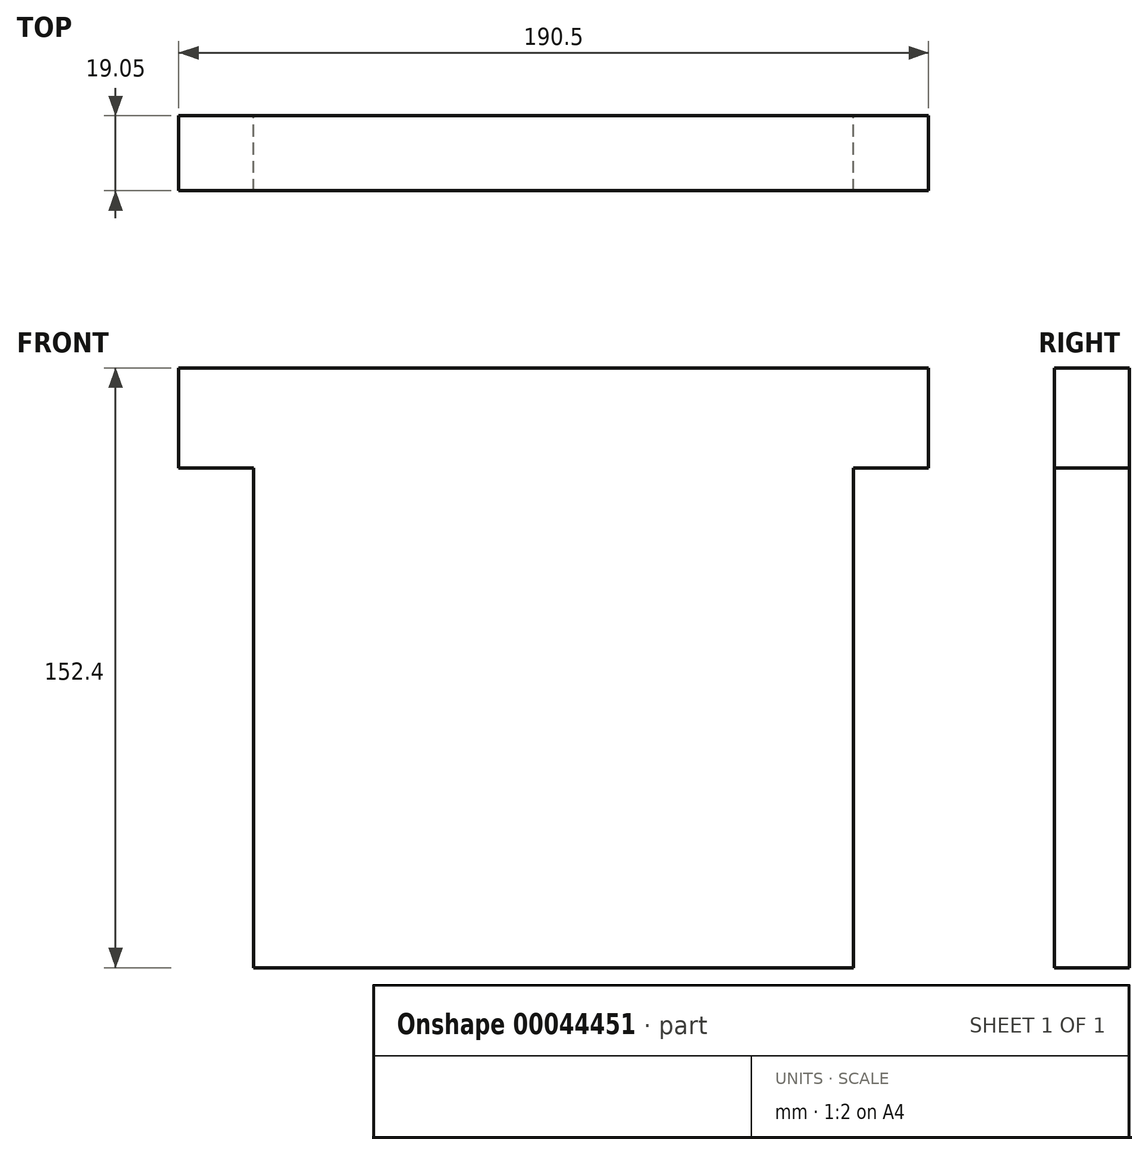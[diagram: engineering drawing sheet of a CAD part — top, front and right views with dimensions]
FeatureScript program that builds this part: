
annotation { "Feature Type Name" : "Feature", "Feature Type Description" : "" }
export const myFeature = defineFeature(function(context is Context, id is Id, definition is map)
    precondition{}
    {
        {
            var Q0;
            Q0=qCreatedBy(makeId("Front.planeOp"),FACE);
            var sketch = newSketch(context, id + "F0", { "sketchPlane" : qUnion([Q0])});
            skLineSegment(sketch, "E0.bottom", {"start": v(-66.37, 67.72) * mm, "end": v(86.03, 67.72) * mm});
            skLineSegment(sketch, "E0.top", {"start": v(-66.37, -84.68) * mm, "end": v(86.03, -84.68) * mm});
            skLineSegment(sketch, "E0.left", {"start": v(-66.37, 67.72) * mm, "end": v(-66.37, -84.68) * mm});
            skLineSegment(sketch, "E0.right", {"start": v(86.03, 67.72) * mm, "end": v(86.03, -84.68) * mm});
            skLineSegment(sketch, "E1.bottom", {"start": v(-66.37, 67.72) * mm, "end": v(-85.42, 67.72) * mm});
            skLineSegment(sketch, "E1.top", {"start": v(-66.37, 42.32) * mm, "end": v(-85.42, 42.32) * mm});
            skLineSegment(sketch, "E1.left", {"start": v(-66.37, 67.72) * mm, "end": v(-66.37, 42.32) * mm});
            skLineSegment(sketch, "E1.right", {"start": v(-85.42, 67.72) * mm, "end": v(-85.42, 42.32) * mm});
            skLineSegment(sketch, "E2.bottom", {"start": v(86.03, 67.72) * mm, "end": v(105.08, 67.72) * mm});
            skLineSegment(sketch, "E2.top", {"start": v(86.03, 42.32) * mm, "end": v(105.08, 42.32) * mm});
            skLineSegment(sketch, "E2.left", {"start": v(86.03, 67.72) * mm, "end": v(86.03, 42.32) * mm});
            skLineSegment(sketch, "E2.right", {"start": v(105.08, 67.72) * mm, "end": v(105.08, 42.32) * mm});
            skSolve(sketch);
        }
        {
            var Q0;
            Q0=makeQuery(id+"F0.imprint","IMPRINT",FACE,{"disambiguationData":[TD([[makeQuery(id+"F0.imprint","IMPRINT",EDGE,{"derivedFrom":sQuery(id+"F0.wireOp",EDGE,"E1.bottom")}),1.0]])]});
            var Q1;
            Q1=makeQuery(id+"F0.imprint","IMPRINT",FACE,{"disambiguationData":[TD([[makeQuery(id+"F0.imprint","IMPRINT",EDGE,{"derivedFrom":sQuery(id+"F0.wireOp",EDGE,"E0.bottom")}),-1.0]])]});
            var Q2;
            Q2=makeQuery(id+"F0.imprint","IMPRINT",FACE,{"disambiguationData":[TD([[makeQuery(id+"F0.imprint","IMPRINT",EDGE,{"derivedFrom":sQuery(id+"F0.wireOp",EDGE,"E2.bottom")}),-1.0]])]});
            extrude(context, id + "F1", {"entities" : qUnion([Q0, Q1, Q2]), "depth" : 19.05 * mm});
        }
    });
